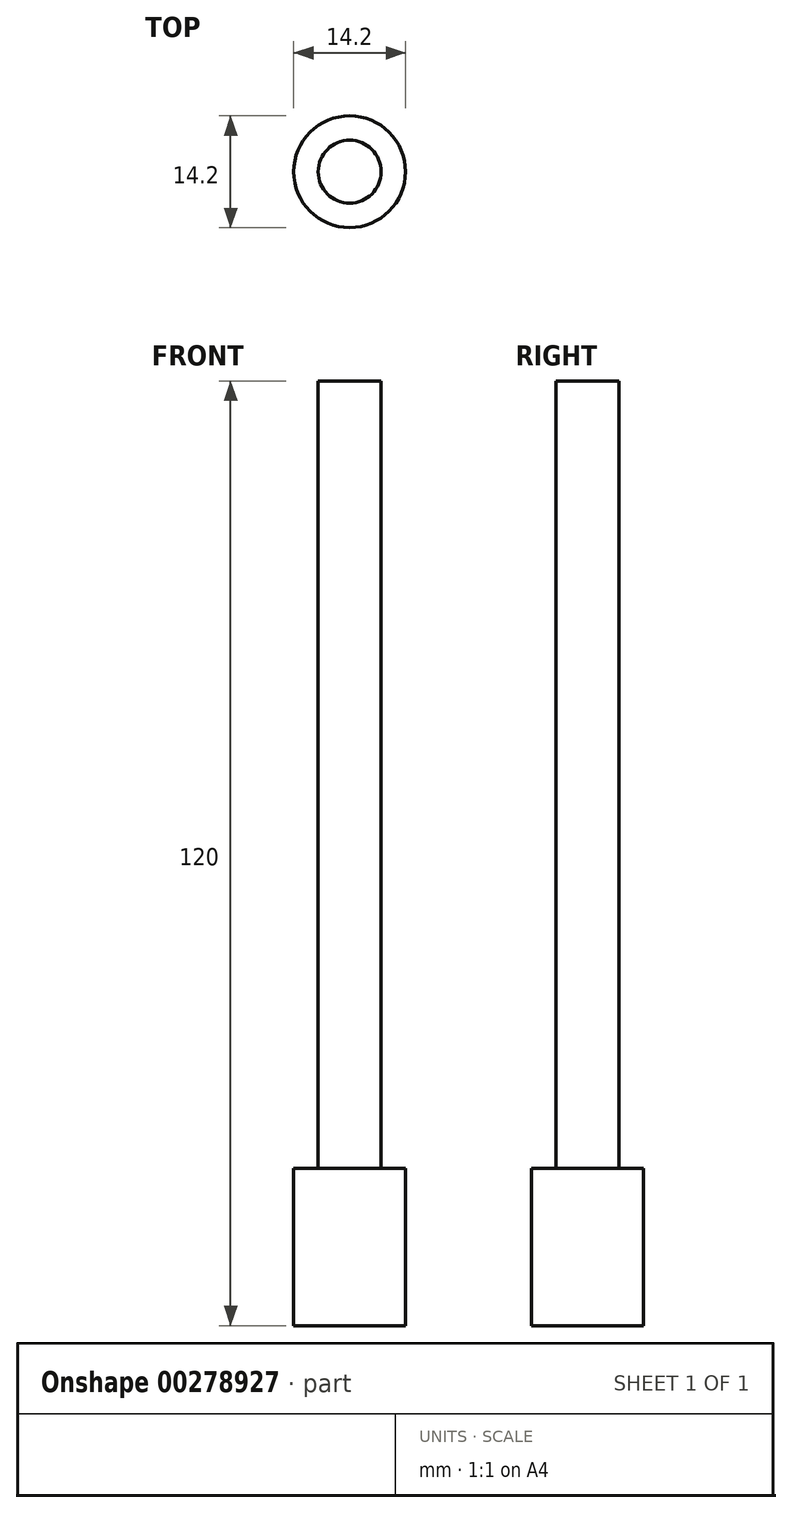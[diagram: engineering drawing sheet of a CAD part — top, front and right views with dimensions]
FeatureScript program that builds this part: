
annotation { "Feature Type Name" : "Feature", "Feature Type Description" : "" }
export const myFeature = defineFeature(function(context is Context, id is Id, definition is map)
    precondition{}
    {
        {
            var Q0;
            Q0=qCreatedBy(makeId("Front.planeOp"),FACE);
            var sketch = newSketch(context, id + "F0", { "sketchPlane" : qUnion([Q0])});
            skLineSegment(sketch, "E0", {"start": v(0, 0) * mm, "end": v(7.1, 0) * mm});
            skLineSegment(sketch, "E1", {"start": v(7.1, 0) * mm, "end": v(7.1, 20) * mm});
            skLineSegment(sketch, "E2", {"start": v(7.1, 20) * mm, "end": v(4, 20) * mm});
            skLineSegment(sketch, "E3", {"start": v(4, 20) * mm, "end": v(4, 120) * mm});
            skLineSegment(sketch, "E4", {"start": v(4, 120) * mm, "end": v(0, 120) * mm});
            skLineSegment(sketch, "E5", {"start": v(0, 120) * mm, "end": v(0, 0) * mm});
            skSolve(sketch);
        }
        {
            var Q0;
            Q0=makeQuery(id+"F0.imprint","IMPRINT",FACE,{"disambiguationData":[TD([[makeQuery(id+"F0.imprint","IMPRINT",EDGE,{"derivedFrom":sQuery(id+"F0.wireOp",EDGE,"E0")}),1.0]])]});
            var Q1;
            Q1=sQuery(id+"F0.wireOp",EDGE,"E5");
            revolve(context, id + "F1", {"entities" : qUnion([Q0]), "axis" : qUnion([Q1]), "revolveType" : RevolveType.FULL});
        }
    });
